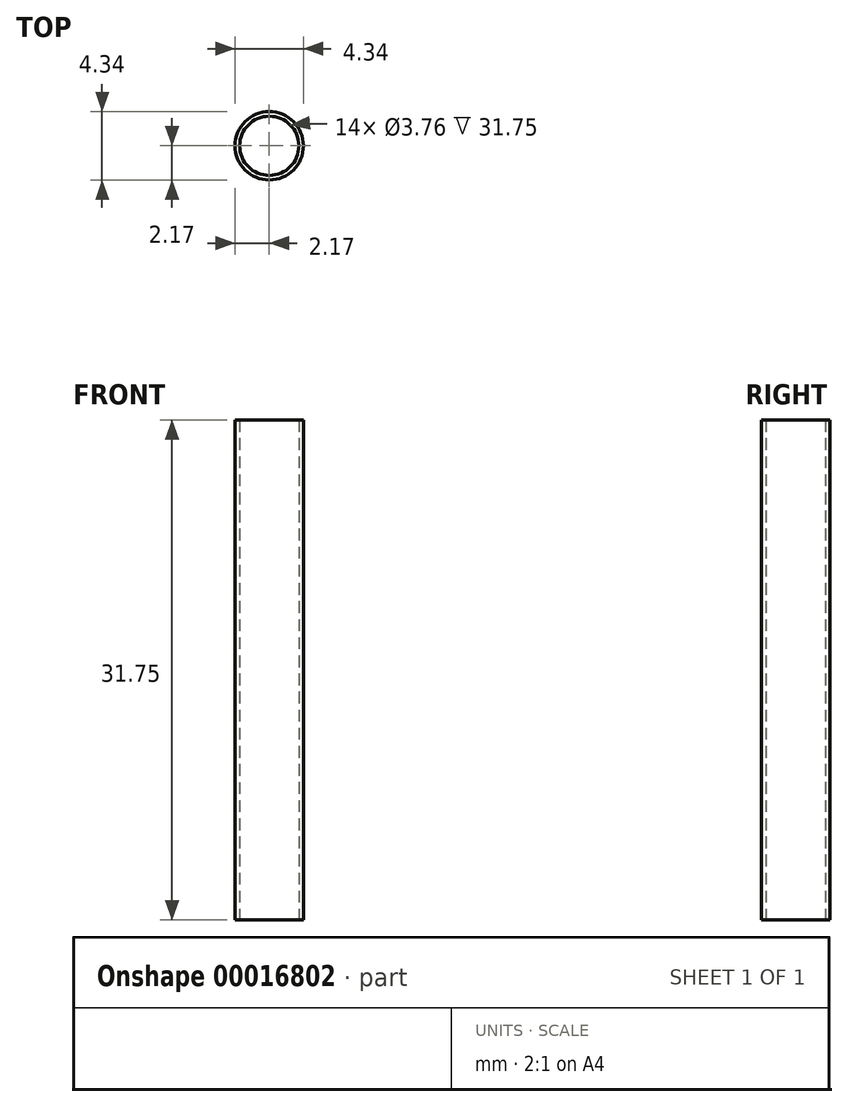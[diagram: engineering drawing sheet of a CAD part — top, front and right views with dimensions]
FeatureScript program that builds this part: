
annotation { "Feature Type Name" : "Feature", "Feature Type Description" : "" }
export const myFeature = defineFeature(function(context is Context, id is Id, definition is map)
    precondition{}
    {
        {
            var Q0;
            Q0=qCreatedBy(makeId("Front.planeOp"),FACE);
            var sketch = newSketch(context, id + "F0", { "sketchPlane" : qUnion([Q0])});
            skLineSegment(sketch, "E0", {"start": v(0, 0) * mm, "end": v(1.88, 0) * mm});
            skLineSegment(sketch, "E1", {"start": v(1.88, 0) * mm, "end": v(1.88, 31.75) * mm});
            skLineSegment(sketch, "E2", {"start": v(1.88, 31.75) * mm, "end": v(2.17, 31.75) * mm});
            skLineSegment(sketch, "E3", {"start": v(2.17, 31.75) * mm, "end": v(2.17, 0) * mm});
            skLineSegment(sketch, "E4", {"start": v(2.17, 0) * mm, "end": v(1.88, 0) * mm});
            skLineSegment(sketch, "E5", {"start": v(0, 0) * mm, "end": v(0, 31.75) * mm});
            skLineSegment(sketch, "E6", {"start": v(0, 31.75) * mm, "end": v(1.88, 31.75) * mm});
            skSolve(sketch);
        }
        {
            var Q0;
            Q0=makeQuery(id+"F0.imprint","IMPRINT",FACE,{"disambiguationData":[TD([[makeQuery(id+"F0.imprint","IMPRINT",EDGE,{"derivedFrom":sQuery(id+"F0.wireOp",EDGE,"E1")}),-1.0]])]});
            var Q1;
            Q1=sQuery(id+"F0.wireOp",EDGE,"E5");
            revolve(context, id + "F1", {"entities" : qUnion([Q0]), "axis" : qUnion([Q1]), "revolveType" : RevolveType.FULL});
        }
    });
